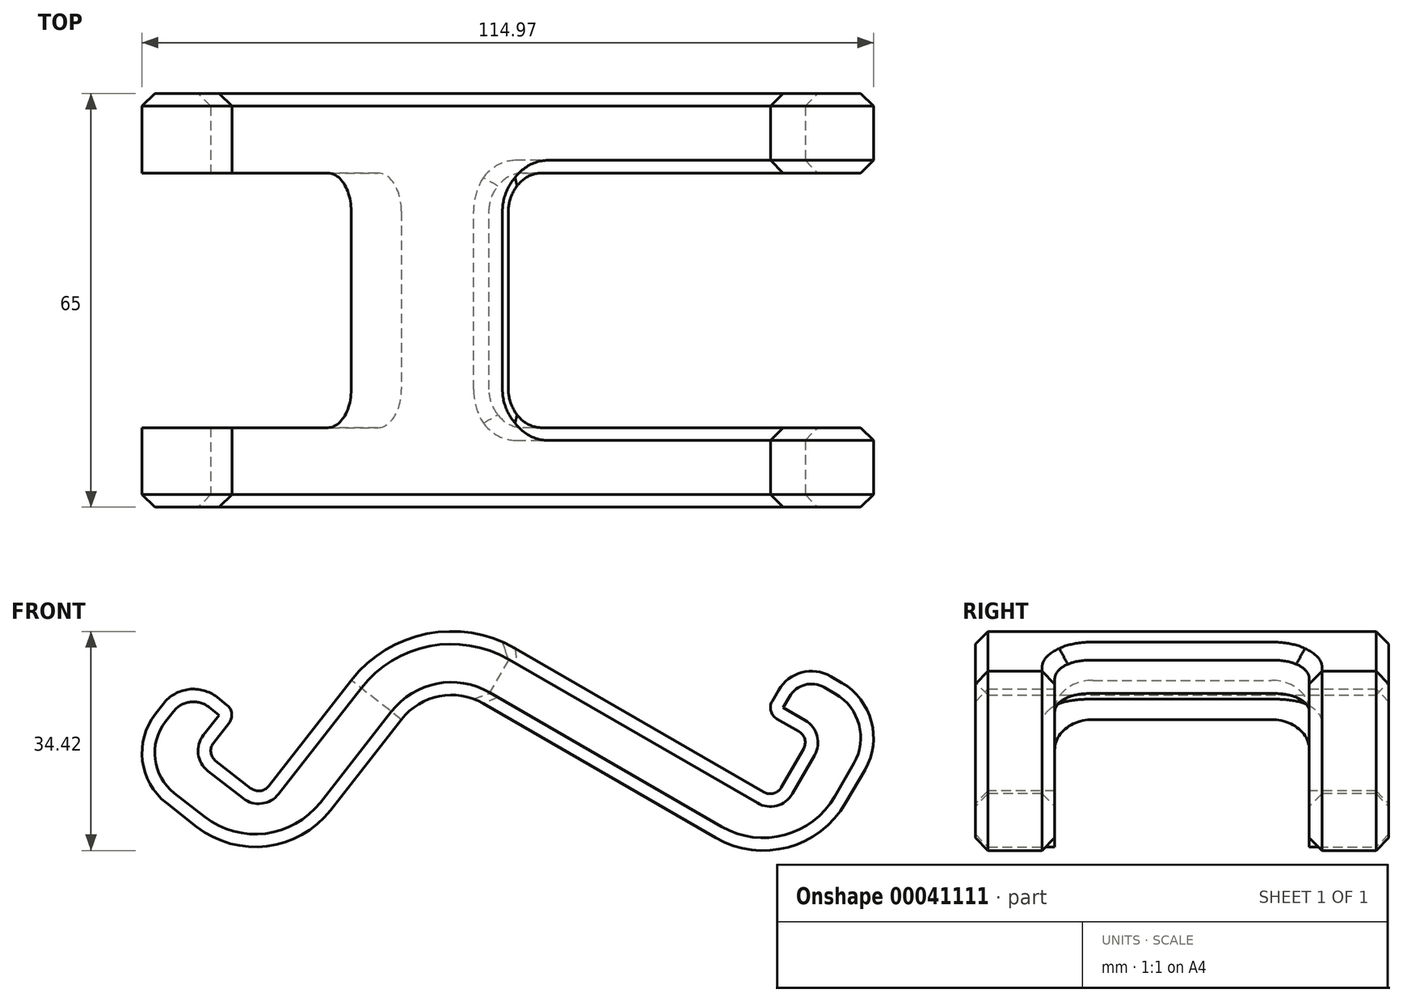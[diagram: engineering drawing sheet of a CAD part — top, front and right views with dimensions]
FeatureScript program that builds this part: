
annotation { "Feature Type Name" : "Feature", "Feature Type Description" : "" }
export const myFeature = defineFeature(function(context is Context, id is Id, definition is map)
    precondition{}
    {
        {
            var Q0;
            Q0=qCreatedBy(makeId("Front.planeOp"),FACE);
            var sketch = newSketch(context, id + "F0", { "sketchPlane" : qUnion([Q0])});
            skLineSegment(sketch, "E0", {"start": v(-41.6, 33.27) * mm, "end": v(-46.52, 26.97) * mm});
            skLineSegment(sketch, "E1", {"start": v(-44.8, 12.93) * mm, "end": v(-40.07, 9.23) * mm});
            skLineSegment(sketch, "E2", {"start": v(-19.01, 11.82) * mm, "end": v(-7.88, 26.07) * mm});
            skLineSegment(sketch, "E3", {"start": v(5, 28.57) * mm, "end": v(41.5, 7.5) * mm});
            skLineSegment(sketch, "E4", {"start": v(62, 13) * mm, "end": v(65, 18.19) * mm});
            skLineSegment(sketch, "E5", {"start": v(61.33, 31.85) * mm, "end": v(54.4, 35.85) * mm});
            skLineSegment(sketch, "E6", {"start": v(54.4, 35.85) * mm, "end": v(49.4, 27.19) * mm});
            skLineSegment(sketch, "E7", {"start": v(49.4, 27.19) * mm, "end": v(56.33, 23.19) * mm});
            skLineSegment(sketch, "E8", {"start": v(56.33, 23.19) * mm, "end": v(50.83, 13.66) * mm});
            skLineSegment(sketch, "E9", {"start": v(50.83, 13.66) * mm, "end": v(10, 37.23) * mm});
            skLineSegment(sketch, "E10", {"start": v(-15.76, 32.23) * mm, "end": v(-29.97, 14.04) * mm});
            skLineSegment(sketch, "E11", {"start": v(-29.97, 14.04) * mm, "end": v(-38.64, 20.8) * mm});
            skLineSegment(sketch, "E12", {"start": v(-38.64, 20.8) * mm, "end": v(-33.71, 27.11) * mm});
            skLineSegment(sketch, "E13", {"start": v(-33.71, 27.11) * mm, "end": v(-41.6, 33.27) * mm});
            skPoint(sketch, "E14.visualSharp", {"position": v(-5.06, 45.93) * mm});
            skArc(sketch, "E14.filletArc", {"start": v(10, 37.23) * mm, "mid": v(-3.82, 39.55) * mm, "end": v(-15.76, 32.23) * mm});
            skPoint(sketch, "E15.visualSharp", {"position": v(-2.53, 32.92) * mm});
            skArc(sketch, "E15.filletArc", {"start": v(5, 28.57) * mm, "mid": v(-1.9, 29.73) * mm, "end": v(-7.88, 26.07) * mm});
            skPoint(sketch, "E16.visualSharp", {"position": v(54.5, 0) * mm});
            skArc(sketch, "E16.filletArc", {"start": v(41.5, 7.5) * mm, "mid": v(52.88, 6) * mm, "end": v(62, 13) * mm});
            skPoint(sketch, "E17.visualSharp", {"position": v(-28.25, 0) * mm});
            skArc(sketch, "E17.filletArc", {"start": v(-40.07, 9.23) * mm, "mid": v(-29, 6.17) * mm, "end": v(-19.01, 11.82) * mm});
            skPoint(sketch, "E18.visualSharp", {"position": v(-52.68, 19.09) * mm});
            skArc(sketch, "E18.filletArc", {"start": v(-46.52, 26.97) * mm, "mid": v(-48.57, 19.6) * mm, "end": v(-44.8, 12.93) * mm});
            skPoint(sketch, "E19.visualSharp", {"position": v(70, 26.85) * mm});
            skArc(sketch, "E19.filletArc", {"start": v(65, 18.19) * mm, "mid": v(65.99, 25.77) * mm, "end": v(61.33, 31.85) * mm});
            skSolve(sketch);
        }
        {
            var Q0;
            Q0 = qSketchRegion(id + "F0", true);
            extrude(context, id + "F1", {"entities" : qUnion([Q0]), "endBound" : BoundingType.SYMMETRIC, "depth" : 65 * mm});
        }
        {
            var Q0;
            Q0=qCreatedBy(makeId("Front.planeOp"),FACE);
            var sketch = newSketch(context, id + "F2", { "sketchPlane" : qUnion([Q0])});
            skLineSegment(sketch, "E20", {"start": v(5, 28.57) * mm, "end": v(54.5, 0) * mm});
            skLineSegment(sketch, "E21", {"start": v(54.5, 0) * mm, "end": v(70, 26.85) * mm});
            skLineSegment(sketch, "E22", {"start": v(70, 26.85) * mm, "end": v(20.5, 55.42) * mm});
            skLineSegment(sketch, "E23", {"start": v(20.5, 55.42) * mm, "end": v(5, 28.57) * mm});
            skLineSegment(sketch, "E24", {"start": v(-7.88, 26.07) * mm, "end": v(-32.3, 45.16) * mm});
            skLineSegment(sketch, "E25", {"start": v(-32.3, 45.16) * mm, "end": v(-52.68, 19.09) * mm});
            skLineSegment(sketch, "E26", {"start": v(-52.68, 19.09) * mm, "end": v(-28.25, 0) * mm});
            skLineSegment(sketch, "E27", {"start": v(-28.25, 0) * mm, "end": v(-7.88, 26.07) * mm});
            skLineSegment(sketch, "E28", {"start": v(-7.88, 26.07) * mm, "end": v(-7.88, 26.07) * mm});
            skLineSegment(sketch, "E29", {"start": v(5, 28.57) * mm, "end": v(5, 28.57) * mm});
            skSolve(sketch);
        }
        {
            var Q0;
            Q0 = qSketchRegion(id + "F2", true);
            extrude(context, id + "F3", {"entities" : qUnion([Q0]), "operationType" : NewBodyOperationType.REMOVE, "endBound" : BoundingType.SYMMETRIC, "oppositeDirection" : true, "depth" : 40 * mm});
        }
        {
            var Q0;
            {var subQ0=sQuery(id+"F0.wireOp",EDGE,"E8");var subQ1=sQuery(id+"F0.wireOp",EDGE,"E9");Q0=makeQuery(id+"F3.boolean.opBoolean","SPLIT",EDGE,{"disambiguationData":[TD([makeQuery(id+"F3.opExtrude","CAP_FACE",FACE,{"disambiguationData":[OSD([sQuery(id+"F2.wireOp",EDGE,"E20"),sQuery(id+"F2.wireOp",EDGE,"E21"),sQuery(id+"F2.wireOp",EDGE,"E22"),sQuery(id+"F2.wireOp",EDGE,"E23")])],"isStart":false})])],"derivedFrom":makeQuery(id+"F1.opExtrude","SWEPT_EDGE",EDGE,{"disambiguationData":[OSD([subQ0,subQ1])]})});}
            var Q1;
            {var subQ0=sQuery(id+"F0.wireOp",EDGE,"E8");var subQ1=sQuery(id+"F0.wireOp",EDGE,"E9");Q1=makeQuery(id+"F3.boolean.opBoolean","SPLIT",EDGE,{"disambiguationData":[TD([makeQuery(id+"F3.opExtrude","CAP_FACE",FACE,{"disambiguationData":[OSD([sQuery(id+"F2.wireOp",EDGE,"E20"),sQuery(id+"F2.wireOp",EDGE,"E21"),sQuery(id+"F2.wireOp",EDGE,"E22"),sQuery(id+"F2.wireOp",EDGE,"E23")])],"isStart":true})])],"derivedFrom":makeQuery(id+"F1.opExtrude","SWEPT_EDGE",EDGE,{"disambiguationData":[OSD([subQ0,subQ1])]})});}
            var Q2;
            {var subQ0=sQuery(id+"F0.wireOp",EDGE,"E7");var subQ1=sQuery(id+"F0.wireOp",EDGE,"E8");Q2=makeQuery(id+"F3.boolean.opBoolean","SPLIT",EDGE,{"disambiguationData":[TD([makeQuery(id+"F3.opExtrude","CAP_FACE",FACE,{"disambiguationData":[OSD([sQuery(id+"F2.wireOp",EDGE,"E20"),sQuery(id+"F2.wireOp",EDGE,"E21"),sQuery(id+"F2.wireOp",EDGE,"E22"),sQuery(id+"F2.wireOp",EDGE,"E23")])],"isStart":true})])],"derivedFrom":makeQuery(id+"F1.opExtrude","SWEPT_EDGE",EDGE,{"disambiguationData":[OSD([subQ0,subQ1])]})});}
            var Q3;
            {var subQ0=sQuery(id+"F0.wireOp",EDGE,"E7");var subQ1=sQuery(id+"F0.wireOp",EDGE,"E8");Q3=makeQuery(id+"F3.boolean.opBoolean","SPLIT",EDGE,{"disambiguationData":[TD([makeQuery(id+"F3.opExtrude","CAP_FACE",FACE,{"disambiguationData":[OSD([sQuery(id+"F2.wireOp",EDGE,"E20"),sQuery(id+"F2.wireOp",EDGE,"E21"),sQuery(id+"F2.wireOp",EDGE,"E22"),sQuery(id+"F2.wireOp",EDGE,"E23")])],"isStart":false})])],"derivedFrom":makeQuery(id+"F1.opExtrude","SWEPT_EDGE",EDGE,{"disambiguationData":[OSD([subQ0,subQ1])]})});}
            var Q4;
            {var subQ0=sQuery(id+"F0.wireOp",EDGE,"E10");var subQ1=sQuery(id+"F0.wireOp",EDGE,"E11");Q4=makeQuery(id+"F3.boolean.opBoolean","SPLIT",EDGE,{"disambiguationData":[TD([makeQuery(id+"F3.opExtrude","CAP_FACE",FACE,{"disambiguationData":[OSD([sQuery(id+"F2.wireOp",EDGE,"E24"),sQuery(id+"F2.wireOp",EDGE,"E25"),sQuery(id+"F2.wireOp",EDGE,"E26"),sQuery(id+"F2.wireOp",EDGE,"E27")])],"isStart":true})])],"derivedFrom":makeQuery(id+"F1.opExtrude","SWEPT_EDGE",EDGE,{"disambiguationData":[OSD([subQ0,subQ1])]})});}
            var Q5;
            {var subQ0=sQuery(id+"F0.wireOp",EDGE,"E10");var subQ1=sQuery(id+"F0.wireOp",EDGE,"E11");Q5=makeQuery(id+"F3.boolean.opBoolean","SPLIT",EDGE,{"disambiguationData":[TD([makeQuery(id+"F3.opExtrude","CAP_FACE",FACE,{"disambiguationData":[OSD([sQuery(id+"F2.wireOp",EDGE,"E24"),sQuery(id+"F2.wireOp",EDGE,"E25"),sQuery(id+"F2.wireOp",EDGE,"E26"),sQuery(id+"F2.wireOp",EDGE,"E27")])],"isStart":false})])],"derivedFrom":makeQuery(id+"F1.opExtrude","SWEPT_EDGE",EDGE,{"disambiguationData":[OSD([subQ0,subQ1])]})});}
            var Q6;
            {var subQ0=sQuery(id+"F0.wireOp",EDGE,"E11");var subQ1=sQuery(id+"F0.wireOp",EDGE,"E12");Q6=makeQuery(id+"F3.boolean.opBoolean","SPLIT",EDGE,{"disambiguationData":[TD([makeQuery(id+"F3.opExtrude","CAP_FACE",FACE,{"disambiguationData":[OSD([sQuery(id+"F2.wireOp",EDGE,"E24"),sQuery(id+"F2.wireOp",EDGE,"E25"),sQuery(id+"F2.wireOp",EDGE,"E26"),sQuery(id+"F2.wireOp",EDGE,"E27")])],"isStart":true})])],"derivedFrom":makeQuery(id+"F1.opExtrude","SWEPT_EDGE",EDGE,{"disambiguationData":[OSD([subQ0,subQ1])]})});}
            var Q7;
            {var subQ0=sQuery(id+"F0.wireOp",EDGE,"E12");var subQ1=sQuery(id+"F0.wireOp",EDGE,"E13");Q7=makeQuery(id+"F3.boolean.opBoolean","SPLIT",EDGE,{"disambiguationData":[TD([makeQuery(id+"F3.opExtrude","CAP_FACE",FACE,{"disambiguationData":[OSD([sQuery(id+"F2.wireOp",EDGE,"E24"),sQuery(id+"F2.wireOp",EDGE,"E25"),sQuery(id+"F2.wireOp",EDGE,"E26"),sQuery(id+"F2.wireOp",EDGE,"E27")])],"isStart":true})])],"derivedFrom":makeQuery(id+"F1.opExtrude","SWEPT_EDGE",EDGE,{"disambiguationData":[OSD([subQ0,subQ1])]})});}
            var Q8;
            {var subQ0=sQuery(id+"F0.wireOp",EDGE,"E12");var subQ1=sQuery(id+"F0.wireOp",EDGE,"E13");Q8=makeQuery(id+"F3.boolean.opBoolean","SPLIT",EDGE,{"disambiguationData":[TD([makeQuery(id+"F3.opExtrude","CAP_FACE",FACE,{"disambiguationData":[OSD([sQuery(id+"F2.wireOp",EDGE,"E24"),sQuery(id+"F2.wireOp",EDGE,"E25"),sQuery(id+"F2.wireOp",EDGE,"E26"),sQuery(id+"F2.wireOp",EDGE,"E27")])],"isStart":false})])],"derivedFrom":makeQuery(id+"F1.opExtrude","SWEPT_EDGE",EDGE,{"disambiguationData":[OSD([subQ0,subQ1])]})});}
            var Q9;
            {var subQ0=sQuery(id+"F0.wireOp",EDGE,"E6");var subQ1=sQuery(id+"F0.wireOp",EDGE,"E7");Q9=makeQuery(id+"F3.boolean.opBoolean","SPLIT",EDGE,{"disambiguationData":[TD([makeQuery(id+"F3.opExtrude","CAP_FACE",FACE,{"disambiguationData":[OSD([sQuery(id+"F2.wireOp",EDGE,"E20"),sQuery(id+"F2.wireOp",EDGE,"E21"),sQuery(id+"F2.wireOp",EDGE,"E22"),sQuery(id+"F2.wireOp",EDGE,"E23")])],"isStart":false})])],"derivedFrom":makeQuery(id+"F1.opExtrude","SWEPT_EDGE",EDGE,{"disambiguationData":[OSD([subQ0,subQ1])]})});}
            var Q10;
            {var subQ0=sQuery(id+"F0.wireOp",EDGE,"E6");var subQ1=sQuery(id+"F0.wireOp",EDGE,"E7");Q10=makeQuery(id+"F3.boolean.opBoolean","SPLIT",EDGE,{"disambiguationData":[TD([makeQuery(id+"F3.opExtrude","CAP_FACE",FACE,{"disambiguationData":[OSD([sQuery(id+"F2.wireOp",EDGE,"E20"),sQuery(id+"F2.wireOp",EDGE,"E21"),sQuery(id+"F2.wireOp",EDGE,"E22"),sQuery(id+"F2.wireOp",EDGE,"E23")])],"isStart":true})])],"derivedFrom":makeQuery(id+"F1.opExtrude","SWEPT_EDGE",EDGE,{"disambiguationData":[OSD([subQ0,subQ1])]})});}
            var Q11;
            {var subQ0=sQuery(id+"F0.wireOp",EDGE,"E11");var subQ1=sQuery(id+"F0.wireOp",EDGE,"E12");Q11=makeQuery(id+"F3.boolean.opBoolean","SPLIT",EDGE,{"disambiguationData":[TD([makeQuery(id+"F3.opExtrude","CAP_FACE",FACE,{"disambiguationData":[OSD([sQuery(id+"F2.wireOp",EDGE,"E24"),sQuery(id+"F2.wireOp",EDGE,"E25"),sQuery(id+"F2.wireOp",EDGE,"E26"),sQuery(id+"F2.wireOp",EDGE,"E27")])],"isStart":false})])],"derivedFrom":makeQuery(id+"F1.opExtrude","SWEPT_EDGE",EDGE,{"disambiguationData":[OSD([subQ0,subQ1])]})});}
            fillet(context, id + "F4", {"entities" : qUnion([Q0, Q1, Q2, Q3, Q4, Q5, Q6, Q7, Q8, Q9, Q10, Q11]), "radius" : 2 * mm, "tangentPropagation" : true, "allowEdgeOverflow" : false});
        }
        {
            var Q0;
            {var subQ0=sQuery(id+"F0.wireOp",EDGE,"E0");var subQ1=sQuery(id+"F0.wireOp",EDGE,"E13");Q0=makeQuery(id+"F3.boolean.opBoolean","SPLIT",EDGE,{"disambiguationData":[TD([makeQuery(id+"F3.opExtrude","CAP_FACE",FACE,{"disambiguationData":[OSD([sQuery(id+"F2.wireOp",EDGE,"E24"),sQuery(id+"F2.wireOp",EDGE,"E25"),sQuery(id+"F2.wireOp",EDGE,"E26"),sQuery(id+"F2.wireOp",EDGE,"E27")])],"isStart":true})])],"derivedFrom":makeQuery(id+"F1.opExtrude","SWEPT_EDGE",EDGE,{"disambiguationData":[OSD([subQ0,subQ1])]})});}
            var Q1;
            {var subQ0=sQuery(id+"F0.wireOp",EDGE,"E0");var subQ1=sQuery(id+"F0.wireOp",EDGE,"E13");Q1=makeQuery(id+"F3.boolean.opBoolean","SPLIT",EDGE,{"disambiguationData":[TD([makeQuery(id+"F3.opExtrude","CAP_FACE",FACE,{"disambiguationData":[OSD([sQuery(id+"F2.wireOp",EDGE,"E24"),sQuery(id+"F2.wireOp",EDGE,"E25"),sQuery(id+"F2.wireOp",EDGE,"E26"),sQuery(id+"F2.wireOp",EDGE,"E27")])],"isStart":false})])],"derivedFrom":makeQuery(id+"F1.opExtrude","SWEPT_EDGE",EDGE,{"disambiguationData":[OSD([subQ0,subQ1])]})});}
            var Q2;
            {var subQ0=sQuery(id+"F0.wireOp",EDGE,"E5");var subQ1=sQuery(id+"F0.wireOp",EDGE,"E6");Q2=makeQuery(id+"F3.boolean.opBoolean","SPLIT",EDGE,{"disambiguationData":[TD([makeQuery(id+"F3.opExtrude","CAP_FACE",FACE,{"disambiguationData":[OSD([sQuery(id+"F2.wireOp",EDGE,"E20"),sQuery(id+"F2.wireOp",EDGE,"E21"),sQuery(id+"F2.wireOp",EDGE,"E22"),sQuery(id+"F2.wireOp",EDGE,"E23")])],"isStart":false})])],"derivedFrom":makeQuery(id+"F1.opExtrude","SWEPT_EDGE",EDGE,{"disambiguationData":[OSD([subQ0,subQ1])]})});}
            var Q3;
            {var subQ0=sQuery(id+"F0.wireOp",EDGE,"E5");var subQ1=sQuery(id+"F0.wireOp",EDGE,"E6");Q3=makeQuery(id+"F3.boolean.opBoolean","SPLIT",EDGE,{"disambiguationData":[TD([makeQuery(id+"F3.opExtrude","CAP_FACE",FACE,{"disambiguationData":[OSD([sQuery(id+"F2.wireOp",EDGE,"E20"),sQuery(id+"F2.wireOp",EDGE,"E21"),sQuery(id+"F2.wireOp",EDGE,"E22"),sQuery(id+"F2.wireOp",EDGE,"E23")])],"isStart":true})])],"derivedFrom":makeQuery(id+"F1.opExtrude","SWEPT_EDGE",EDGE,{"disambiguationData":[OSD([subQ0,subQ1])]})});}
            fillet(context, id + "F5", {"entities" : qUnion([Q0, Q1, Q2, Q3]), "radius" : 6 * mm, "tangentPropagation" : true, "allowEdgeOverflow" : false});
        }
        {
            var Q0;
            Q0=makeQuery(id+"F3.boolean.opBoolean","COPY",EDGE,{"derivedFrom":makeQuery(id+"F3.opExtrude","CAP_EDGE",EDGE,{"disambiguationData":[OSD([sQuery(id+"F2.wireOp",EDGE,"E23")])],"isStart":true})});
            var Q1;
            Q1=makeQuery(id+"F3.boolean.opBoolean","COPY",EDGE,{"derivedFrom":makeQuery(id+"F3.opExtrude","CAP_EDGE",EDGE,{"disambiguationData":[OSD([sQuery(id+"F2.wireOp",EDGE,"E23")])],"isStart":false})});
            var Q2;
            Q2=makeQuery(id+"F3.boolean.opBoolean","COPY",EDGE,{"derivedFrom":makeQuery(id+"F3.opExtrude","CAP_EDGE",EDGE,{"disambiguationData":[OSD([sQuery(id+"F2.wireOp",EDGE,"E24")])],"isStart":true})});
            var Q3;
            Q3=makeQuery(id+"F3.boolean.opBoolean","COPY",EDGE,{"derivedFrom":makeQuery(id+"F3.opExtrude","CAP_EDGE",EDGE,{"disambiguationData":[OSD([sQuery(id+"F2.wireOp",EDGE,"E24")])],"isStart":false})});
            fillet(context, id + "F6", {"entities" : qUnion([Q0, Q1, Q2, Q3]), "radius" : 6 * mm, "tangentPropagation" : true, "allowEdgeOverflow" : false});
        }
        {
            var Q0;
            Q0=makeQuery(id+"F3.boolean.opBoolean","INTERSECT",EDGE,{"derivedFrom":[makeQuery(id+"F1.opExtrude","SWEPT_FACE",FACE,{"disambiguationData":[OSD([sQuery(id+"F0.wireOp",EDGE,"E9")])]}),makeQuery(id+"F3.opExtrude","CAP_FACE",FACE,{"disambiguationData":[OSD([sQuery(id+"F2.wireOp",EDGE,"E20"),sQuery(id+"F2.wireOp",EDGE,"E21"),sQuery(id+"F2.wireOp",EDGE,"E22"),sQuery(id+"F2.wireOp",EDGE,"E23")])],"isStart":true})]});
            var Q1;
            Q1=makeQuery(id+"F3.boolean.opBoolean","INTERSECT",EDGE,{"derivedFrom":[makeQuery(id+"F1.opExtrude","SWEPT_FACE",FACE,{"disambiguationData":[OSD([sQuery(id+"F0.wireOp",EDGE,"E8")])]}),makeQuery(id+"F3.opExtrude","CAP_FACE",FACE,{"disambiguationData":[OSD([sQuery(id+"F2.wireOp",EDGE,"E20"),sQuery(id+"F2.wireOp",EDGE,"E21"),sQuery(id+"F2.wireOp",EDGE,"E22"),sQuery(id+"F2.wireOp",EDGE,"E23")])],"isStart":true})]});
            var Q2;
            {var subQ0=sQuery(id+"F0.wireOp",EDGE,"E8");var subQ1=sQuery(id+"F0.wireOp",EDGE,"E9");var subQ2=makeQuery(id+"F3.opExtrude","CAP_FACE",FACE,{"disambiguationData":[OSD([sQuery(id+"F2.wireOp",EDGE,"E20"),sQuery(id+"F2.wireOp",EDGE,"E21"),sQuery(id+"F2.wireOp",EDGE,"E22"),sQuery(id+"F2.wireOp",EDGE,"E23")])],"isStart":true});Q2=makeQuery(id+"F4.opFillet","BLEND_EDGE",EDGE,{"blendedFrom":[makeQuery(id+"F3.boolean.opBoolean","SPLIT",EDGE,{"disambiguationData":[TD([subQ2])],"derivedFrom":makeQuery(id+"F1.opExtrude","SWEPT_EDGE",EDGE,{"disambiguationData":[OSD([subQ0,subQ1])]})}),makeQuery(id+"F3.boolean.opBoolean","COPY",FACE,{"derivedFrom":subQ2})],"blendedInto":[makeQuery(id+"F3.boolean.opBoolean","COPY",FACE,{"derivedFrom":subQ2})]});}
            var Q3;
            Q3=makeQuery(id+"F6.opFillet","BLEND_EDGE",EDGE,{"blendedFrom":[makeQuery(id+"F3.boolean.opBoolean","COPY",EDGE,{"derivedFrom":makeQuery(id+"F3.opExtrude","CAP_EDGE",EDGE,{"disambiguationData":[OSD([sQuery(id+"F2.wireOp",EDGE,"E23")])],"isStart":true})}),makeQuery(id+"F1.opExtrude","SWEPT_FACE",FACE,{"disambiguationData":[OSD([sQuery(id+"F0.wireOp",EDGE,"E9")])]})],"blendedInto":[makeQuery(id+"F1.opExtrude","SWEPT_FACE",FACE,{"disambiguationData":[OSD([sQuery(id+"F0.wireOp",EDGE,"E9")])]})]});
            var Q4;
            Q4=makeQuery(id+"F3.boolean.opBoolean","INTERSECT",EDGE,{"derivedFrom":[makeQuery(id+"F1.opExtrude","SWEPT_FACE",FACE,{"disambiguationData":[OSD([sQuery(id+"F0.wireOp",EDGE,"E9")])]}),makeQuery(id+"F3.opExtrude","SWEPT_FACE",FACE,{"disambiguationData":[OSD([sQuery(id+"F2.wireOp",EDGE,"E23")])]})]});
            var Q5;
            Q5=makeQuery(id+"F6.opFillet","BLEND_EDGE",EDGE,{"blendedFrom":[makeQuery(id+"F3.boolean.opBoolean","COPY",EDGE,{"derivedFrom":makeQuery(id+"F3.opExtrude","CAP_EDGE",EDGE,{"disambiguationData":[OSD([sQuery(id+"F2.wireOp",EDGE,"E23")])],"isStart":false})}),makeQuery(id+"F1.opExtrude","SWEPT_FACE",FACE,{"disambiguationData":[OSD([sQuery(id+"F0.wireOp",EDGE,"E9")])]})],"blendedInto":[makeQuery(id+"F1.opExtrude","SWEPT_FACE",FACE,{"disambiguationData":[OSD([sQuery(id+"F0.wireOp",EDGE,"E9")])]})]});
            var Q6;
            Q6=makeQuery(id+"F3.boolean.opBoolean","INTERSECT",EDGE,{"derivedFrom":[makeQuery(id+"F1.opExtrude","SWEPT_FACE",FACE,{"disambiguationData":[OSD([sQuery(id+"F0.wireOp",EDGE,"E9")])]}),makeQuery(id+"F3.opExtrude","CAP_FACE",FACE,{"disambiguationData":[OSD([sQuery(id+"F2.wireOp",EDGE,"E20"),sQuery(id+"F2.wireOp",EDGE,"E21"),sQuery(id+"F2.wireOp",EDGE,"E22"),sQuery(id+"F2.wireOp",EDGE,"E23")])],"isStart":false})]});
            var Q7;
            {var subQ0=sQuery(id+"F0.wireOp",EDGE,"E8");var subQ1=sQuery(id+"F0.wireOp",EDGE,"E9");var subQ2=makeQuery(id+"F3.opExtrude","CAP_FACE",FACE,{"disambiguationData":[OSD([sQuery(id+"F2.wireOp",EDGE,"E20"),sQuery(id+"F2.wireOp",EDGE,"E21"),sQuery(id+"F2.wireOp",EDGE,"E22"),sQuery(id+"F2.wireOp",EDGE,"E23")])],"isStart":false});Q7=makeQuery(id+"F4.opFillet","BLEND_EDGE",EDGE,{"blendedFrom":[makeQuery(id+"F3.boolean.opBoolean","SPLIT",EDGE,{"disambiguationData":[TD([subQ2])],"derivedFrom":makeQuery(id+"F1.opExtrude","SWEPT_EDGE",EDGE,{"disambiguationData":[OSD([subQ0,subQ1])]})}),makeQuery(id+"F3.boolean.opBoolean","COPY",FACE,{"derivedFrom":subQ2})],"blendedInto":[makeQuery(id+"F3.boolean.opBoolean","COPY",FACE,{"derivedFrom":subQ2})]});}
            var Q8;
            Q8=makeQuery(id+"F3.boolean.opBoolean","INTERSECT",EDGE,{"derivedFrom":[makeQuery(id+"F1.opExtrude","SWEPT_FACE",FACE,{"disambiguationData":[OSD([sQuery(id+"F0.wireOp",EDGE,"E8")])]}),makeQuery(id+"F3.opExtrude","CAP_FACE",FACE,{"disambiguationData":[OSD([sQuery(id+"F2.wireOp",EDGE,"E20"),sQuery(id+"F2.wireOp",EDGE,"E21"),sQuery(id+"F2.wireOp",EDGE,"E22"),sQuery(id+"F2.wireOp",EDGE,"E23")])],"isStart":false})]});
            var Q9;
            Q9=makeQuery(id+"F3.boolean.opBoolean","INTERSECT",EDGE,{"derivedFrom":[makeQuery(id+"F1.opExtrude","SWEPT_FACE",FACE,{"disambiguationData":[OSD([sQuery(id+"F0.wireOp",EDGE,"E10")])]}),makeQuery(id+"F3.opExtrude","SWEPT_FACE",FACE,{"disambiguationData":[OSD([sQuery(id+"F2.wireOp",EDGE,"E24")])]})]});
            var Q10;
            Q10=makeQuery(id+"F1.opExtrude","CAP_EDGE",EDGE,{"disambiguationData":[OSD([sQuery(id+"F0.wireOp",EDGE,"E15.filletArc")])],"isStart":false});
            var Q11;
            Q11=makeQuery(id+"F1.opExtrude","CAP_EDGE",EDGE,{"disambiguationData":[OSD([sQuery(id+"F0.wireOp",EDGE,"E15.filletArc")])],"isStart":true});
            chamfer(context, id + "F7", {"entities" : qUnion([Q0, Q1, Q2, Q3, Q4, Q5, Q6, Q7, Q8, Q9, Q10, Q11]), "width" : 2 * mm, "tangentPropagation" : true});
        }
    });
